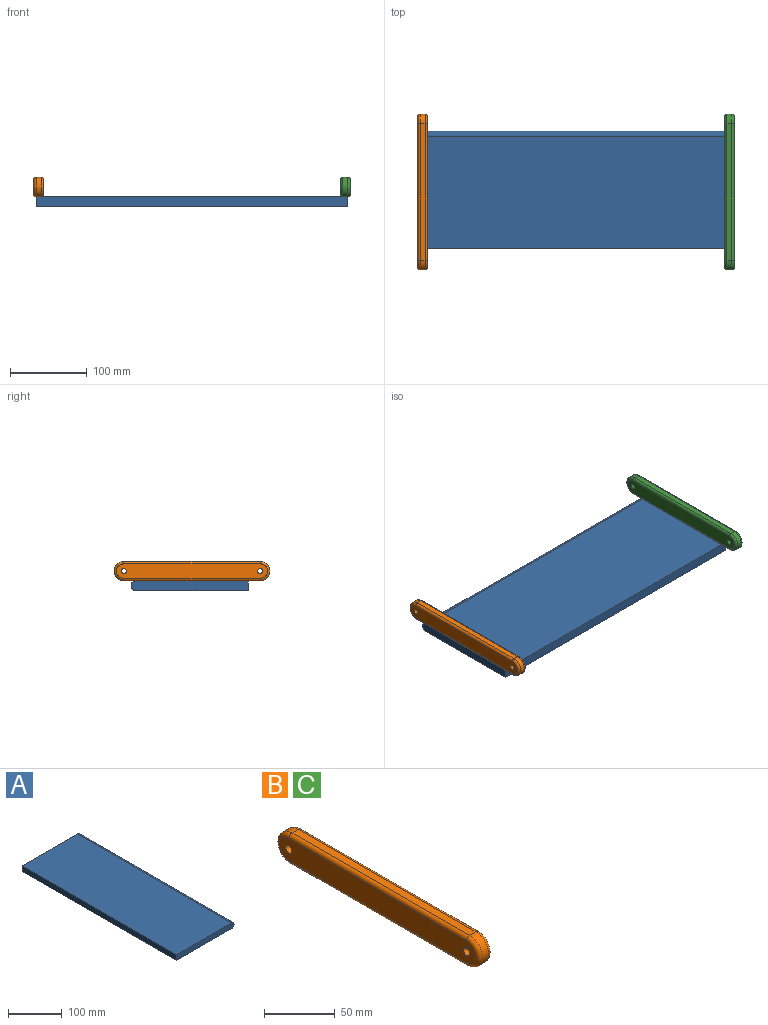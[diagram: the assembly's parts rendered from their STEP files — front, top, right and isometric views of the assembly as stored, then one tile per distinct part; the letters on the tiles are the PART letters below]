
ASSEMBLY  parts=3 mates=2
PART A: 6 faces, bbox 152.4x406.4x12.7 mm
  f0: plane 406.4x12.7mm, normal (-1,0,0), area 5161.3mm2, adj f1,f2,f3,f4
  f1: plane 152.4x12.7mm, normal (0,-1,0), area 1918.2mm2, adj f0,f3,f4,f5
  f2: plane 152.4x12.7mm, normal (0,1,0), area 1918.2mm2, adj f0,f3,f4,f5
  f3: plane 406.4x146.05mm, normal (0,0,1), area 59354.7mm2, adj f0,f1,f2,f5
  f4: plane 406.4x146.05mm, normal (0,0,-1), area 59354.7mm2, adj f0,f1,f2,f5
  f5: cylinder r=6.35mm len=406.4mm, axis (0,-1,0), area 8107.3mm2, adj f1,f2,f3,f4
PART B: 16 faces, bbox 12.7x205.3x27.5 mm
  f0: plane 177.8x6.35mm, normal (0,0,-1), area 1129mm2, adj f4,f5,f11,f15
  f1: plane 177.8x6.35mm, normal (0,0,1), area 1129mm2, adj f4,f5,f8,f12
  f2: plane 196.85x19.05mm, normal (1,0,0), area 3608.8mm2, adj f6,f7,f8,f9,f10,f11
  f3: plane 196.85x19.05mm, normal (-1,0,0), area 3608.8mm2, adj f6,f7,f12,f13,f14,f15
  f4: cylinder r=12.7mm len=25.4mm, axis (-1,0,0), area 253.4mm2, adj f0,f1,f9,f13
  f5: cylinder r=12.7mm len=25.4mm, axis (1,0,0), area 253.4mm2, adj f0,f1,f10,f14
  f6: cylinder r=3.17mm len=12.7mm, axis (1,0,0), area 253.4mm2, adj f2,f3
  f7: cylinder r=3.17mm len=12.7mm, axis (1,0,0), area 253.4mm2, adj f2,f3
  f8: cylinder r=3.17mm len=177.8mm, axis (0,1,0), area 886.7mm2, adj f1,f2,f9,f10
  f9: torus R=9.53mm, axis (1,0,0), area 180.9mm2, adj f2,f4,f8,f11
  f10: torus R=9.53mm, axis (1,0,0), area 180.9mm2, adj f2,f5,f8,f11
  f11: cylinder r=3.17mm len=177.8mm, axis (0,-1,0), area 886.7mm2, adj f0,f2,f9,f10
  f12: cylinder r=3.17mm len=177.8mm, axis (0,-1,0), area 886.7mm2, adj f1,f3,f13,f14
  f13: torus R=9.53mm, axis (1,0,0), area 180.9mm2, adj f3,f4,f12,f15
  f14: torus R=9.53mm, axis (1,0,0), area 180.9mm2, adj f3,f5,f12,f15
  f15: cylinder r=3.17mm len=177.8mm, axis (0,1,0), area 886.7mm2, adj f0,f3,f13,f14
PART C: same geometry as B
PLACE A rot(axis=(0,0,1),90deg) t=(-109.16,-678.42,-489.76)mm
PLACE B t=(-518.73,-707,-477.06)mm
PLACE C t=(-118.68,-707,-477.06)mm
MATE fastened A.f3 <-> B.f0  axis (0,0,1) through (-515.56,-605.4,-477.06)mm
MATE fastened C.f0 <-> A.f3  axis (0,0,-1) through (-109.16,-605.4,-477.06)mm
